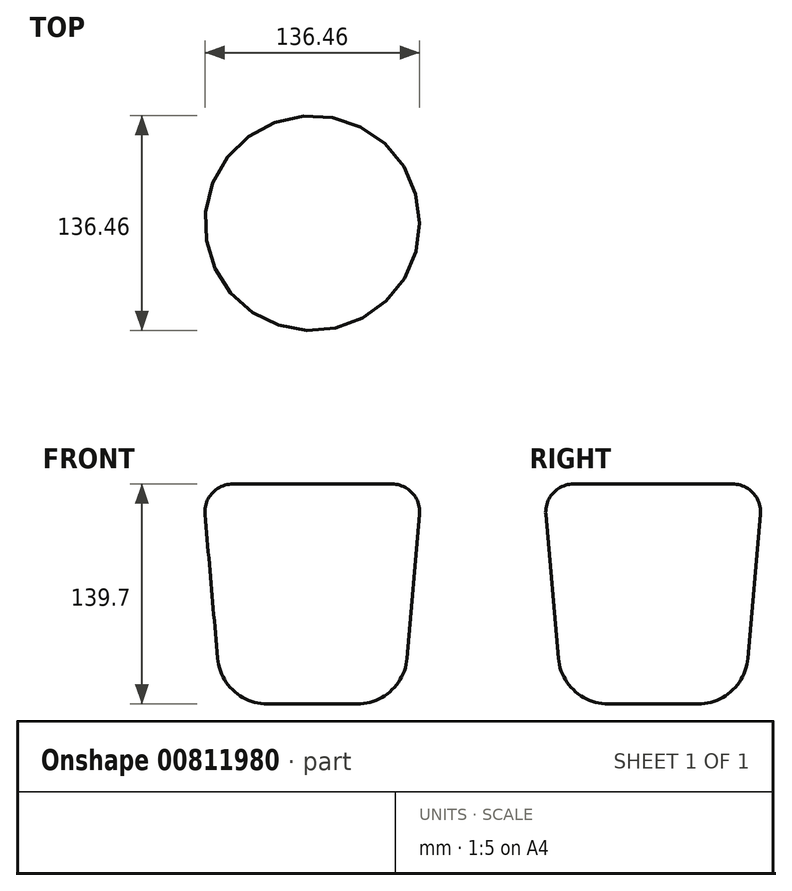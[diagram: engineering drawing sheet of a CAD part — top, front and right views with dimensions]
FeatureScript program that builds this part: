
annotation { "Feature Type Name" : "Feature", "Feature Type Description" : "" }
export const myFeature = defineFeature(function(context is Context, id is Id, definition is map)
    precondition{}
    {
        {
            var Q0;
            Q0=qCreatedBy(makeId("Top.planeOp"),FACE);
            var sketch = newSketch(context, id + "F0", { "sketchPlane" : qUnion([Q0])});
            skCircle(sketch, "E0", {"center": v(0, 0) * mm, "radius": 69.85 * mm});
            skSolve(sketch);
        }
        {
            var Q0;
            Q0 = qSketchRegion(id + "F0", true);
            extrude(context, id + "F1", {"entities" : qUnion([Q0]), "oppositeDirection" : true, "depth" : 139.7 * mm, "offsetDistance" : 25.4 * mm, "hasDraft" : true, "draftAngle" : 5 * degree, "draftPullDirection" : true});
        }
        {
            var Q0;
            Q0=makeQuery(id+"F1.opExtrude","CAP_EDGE",EDGE,{"disambiguationData":[OSD([sQuery(id+"F0.wireOp",EDGE,"E0")])],"isStart":false});
            fillet(context, id + "F2", {"entities" : qUnion([Q0]), "radius" : 31.75 * mm, "tangentPropagation" : true, "allowEdgeOverflow" : false});
        }
        {
            var Q0;
            Q0=makeQuery(id+"F1.opExtrude","CAP_EDGE",EDGE,{"disambiguationData":[OSD([sQuery(id+"F0.wireOp",EDGE,"E0")])],"isStart":true});
            fillet(context, id + "F3", {"entities" : qUnion([Q0]), "radius" : 17.78 * mm, "tangentPropagation" : true, "allowEdgeOverflow" : false});
        }
    });
